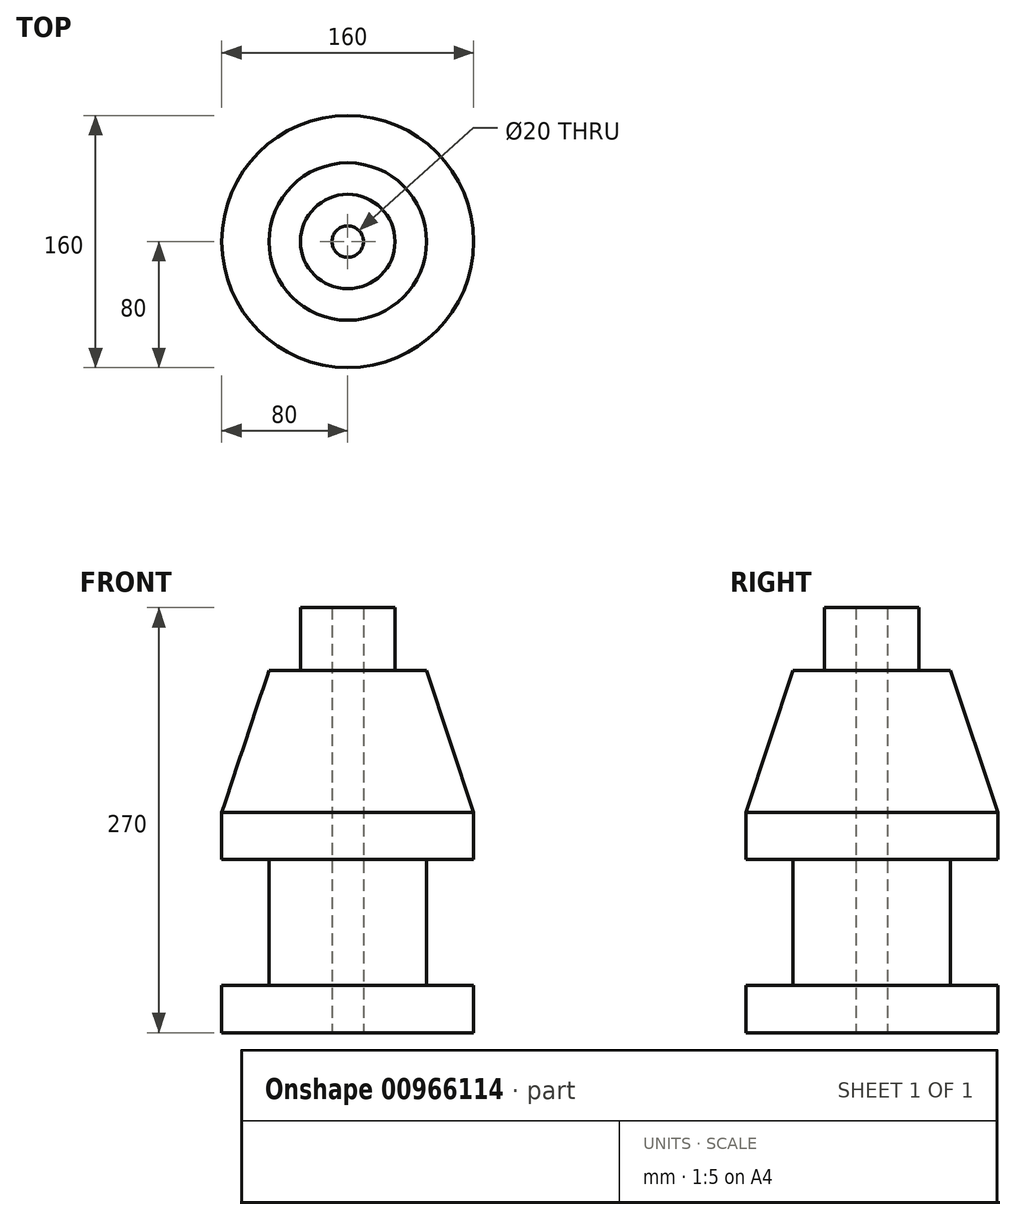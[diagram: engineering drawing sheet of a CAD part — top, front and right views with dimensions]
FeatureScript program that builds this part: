
annotation { "Feature Type Name" : "Feature", "Feature Type Description" : "" }
export const myFeature = defineFeature(function(context is Context, id is Id, definition is map)
    precondition{}
    {
        {
            var Q0;
            Q0=qCreatedBy(makeId("Front.planeOp"),FACE);
            var sketch = newSketch(context, id + "F0", { "sketchPlane" : qUnion([Q0])});
            skLineSegment(sketch, "E0", {"start": v(0, 99.3) * mm, "end": v(0, -119.77) * mm, "construction": true});
            skLineSegment(sketch, "E1", {"start": v(10, 0) * mm, "end": v(10, 270) * mm});
            skLineSegment(sketch, "E2", {"start": v(10, 270) * mm, "end": v(30, 270) * mm});
            skLineSegment(sketch, "E3", {"start": v(30, 270) * mm, "end": v(30, 230) * mm});
            skLineSegment(sketch, "E4", {"start": v(30, 230) * mm, "end": v(50, 230) * mm});
            skLineSegment(sketch, "E5", {"start": v(50, 230) * mm, "end": v(80, 140) * mm});
            skLineSegment(sketch, "E6", {"start": v(80, 140) * mm, "end": v(80, 110) * mm});
            skLineSegment(sketch, "E7", {"start": v(80, 110) * mm, "end": v(50, 110) * mm});
            skLineSegment(sketch, "E8", {"start": v(50, 30) * mm, "end": v(80, 30) * mm});
            skLineSegment(sketch, "E9", {"start": v(10, 0) * mm, "end": v(80, 0) * mm});
            skLineSegment(sketch, "E10", {"start": v(0, 0) * mm, "end": v(0, 308.09) * mm, "construction": true});
            skPoint(sketch, "E11.orphan", {"position": v(30, 110) * mm});
            skPoint(sketch, "E12.orphan", {"position": v(20, 30) * mm});
            skLineSegment(sketch, "E13", {"start": v(50, 30) * mm, "end": v(50, 110) * mm});
            skLineSegment(sketch, "E14", {"start": v(80, 30) * mm, "end": v(80, 0) * mm});
            skSolve(sketch);
        }
        {
            var Q0;
            Q0 = qSketchRegion(id + "F0", true);
            var Q1;
            Q1=sQuery(id+"F0.wireOp",EDGE,"E10");
            revolve(context, id + "F1", {"surfaceOperationType" : NewSurfaceOperationType.NEW, "entities" : qUnion([Q0]), "axis" : qUnion([Q1]), "revolveType" : RevolveType.FULL});
        }
    });
